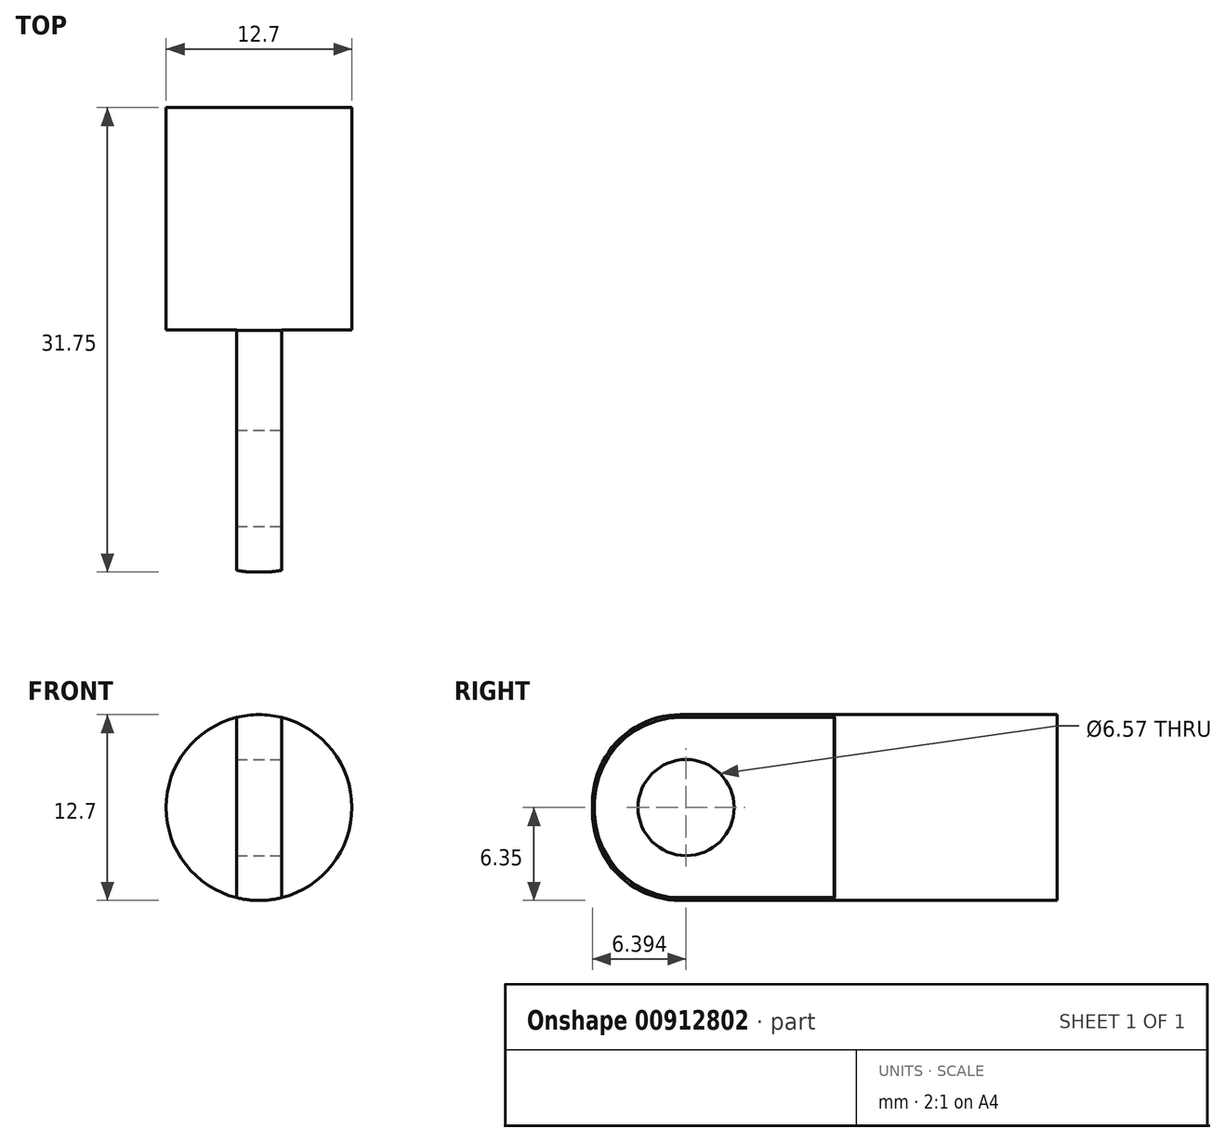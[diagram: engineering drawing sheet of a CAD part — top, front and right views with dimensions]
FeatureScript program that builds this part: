
annotation { "Feature Type Name" : "Feature", "Feature Type Description" : "" }
export const myFeature = defineFeature(function(context is Context, id is Id, definition is map)
    precondition{}
    {
        {
            var Q0;
            Q0=qCreatedBy(makeId("Front.planeOp"),FACE);
            var sketch = newSketch(context, id + "F0", { "sketchPlane" : qUnion([Q0])});
            skCircle(sketch, "E0", {"center": v(0, 0) * mm, "radius": 6.35 * mm});
            skSolve(sketch);
        }
        {
            var Q0;
            Q0 = qSketchRegion(id + "F0", true);
            extrude(context, id + "F1", {"entities" : qUnion([Q0]), "depth" : 31.75 * mm, "offsetDistance" : 25.4 * mm});
        }
        {
            var Q0;
            Q0=makeQuery(id+"F1.opExtrude","CAP_EDGE",EDGE,{"disambiguationData":[OSD([sQuery(id+"F0.wireOp",EDGE,"E0")])],"isStart":false});
            fillet(context, id + "F2", {"entities" : qUnion([Q0]), "radius" : 6.25 * mm, "tangentPropagation" : true, "allowEdgeOverflow" : false});
        }
        {
            var Q0;
            Q0=qCreatedBy(makeId("Top.planeOp"),FACE);
            var sketch = newSketch(context, id + "F3", { "sketchPlane" : qUnion([Q0])});
            skLineSegment(sketch, "E1.bottom", {"start": v(0, -35.56) * mm, "end": v(-1.54, -35.56) * mm});
            skLineSegment(sketch, "E1.top", {"start": v(0, -25.4) * mm, "end": v(-1.54, -25.4) * mm});
            skLineSegment(sketch, "E1.left", {"start": v(0, -35.56) * mm, "end": v(0, -25.4) * mm});
            skLineSegment(sketch, "E1.right", {"start": v(-1.54, -35.56) * mm, "end": v(-1.54, -25.4) * mm});
            skLineSegment(sketch, "E2.MirrorCS", {"start": v(0, -35.56) * mm, "end": v(1.54, -35.56) * mm});
            skLineSegment(sketch, "E3.MirrorCS", {"start": v(1.54, -35.56) * mm, "end": v(1.54, -25.4) * mm});
            skLineSegment(sketch, "E4.MirrorCS", {"start": v(0, -25.4) * mm, "end": v(1.54, -25.4) * mm});
            skLineSegment(sketch, "E5.MirrorCS", {"start": v(0, -15.24) * mm, "end": v(-1.54, -15.24) * mm});
            skLineSegment(sketch, "E6.MirrorCS", {"start": v(0, -15.24) * mm, "end": v(0, -25.4) * mm});
            skLineSegment(sketch, "E7.MirrorCS", {"start": v(-1.54, -15.24) * mm, "end": v(-1.54, -25.4) * mm});
            skLineSegment(sketch, "E8.MirrorCS", {"start": v(1.54, -15.24) * mm, "end": v(1.54, -25.4) * mm});
            skLineSegment(sketch, "E9.MirrorCS", {"start": v(0, -15.24) * mm, "end": v(1.54, -15.24) * mm});
            skSolve(sketch);
        }
        {
            var Q0;
            Q0 = qSketchRegion(id + "F3", true);
            var Q1;
            Q1 = qSketchRegion(id + "F5", true);
            extrude(context, id + "F4", {"entities" : qUnion([Q0, Q1]), "operationType" : NewBodyOperationType.REMOVE, "endBound" : BoundingType.SYMMETRIC, "oppositeDirection" : true, "depth" : 46.28 * mm, "offsetDistance" : 25.4 * mm});
        }
        {
            var Q0;
            Q0=qCreatedBy(makeId("Right.planeOp"),FACE);
            var sketch = newSketch(context, id + "F5", { "sketchPlane" : qUnion([Q0])});
            skCircle(sketch, "E10", {"center": v(-25.5, 0) * mm, "radius": 2.23 * mm});
            skCircle(sketch, "E11", {"center": v(-25.5, 0) * mm, "radius": 2.58 * mm});
            skSolve(sketch);
        }
        {
            var Q0;
            Q0=makeQuery(id+"F5.imprint","IMPRINT",FACE,{"disambiguationData":[TD([[makeQuery(id+"F5.imprint","IMPRINT",EDGE,{"derivedFrom":sQuery(id+"F5.wireOp",EDGE,"E10")}),1.0]])]});
            extrude(context, id + "F6", {"entities" : qUnion([Q0]), "operationType" : NewBodyOperationType.ADD, "endBound" : BoundingType.SYMMETRIC, "depth" : 5.03 * mm, "offsetDistance" : 25.4 * mm});
        }
        {
            var Q0;
            Q0=qCreatedBy(makeId("Top.planeOp"),FACE);
            var sketch = newSketch(context, id + "F7", { "sketchPlane" : qUnion([Q0])});
            skLineSegment(sketch, "E12.bottom", {"start": v(-1.54, -15.2) * mm, "end": v(-9.34, -15.2) * mm});
            skLineSegment(sketch, "E12.top", {"start": v(-1.54, -35.55) * mm, "end": v(-9.34, -35.55) * mm});
            skLineSegment(sketch, "E12.left", {"start": v(-1.54, -15.2) * mm, "end": v(-1.54, -35.55) * mm});
            skLineSegment(sketch, "E12.right", {"start": v(-9.34, -15.2) * mm, "end": v(-9.34, -35.55) * mm});
            skLineSegment(sketch, "E13.MirrorCS", {"start": v(1.54, -15.2) * mm, "end": v(1.54, -35.55) * mm});
            skLineSegment(sketch, "E14.MirrorCS", {"start": v(1.54, -35.55) * mm, "end": v(9.34, -35.55) * mm});
            skLineSegment(sketch, "E15.MirrorCS", {"start": v(1.54, -15.2) * mm, "end": v(9.34, -15.2) * mm});
            skLineSegment(sketch, "E16.MirrorCS", {"start": v(9.34, -15.2) * mm, "end": v(9.34, -35.55) * mm});
            skSolve(sketch);
        }
        {
            var Q0;
            Q0 = qSketchRegion(id + "F0", true);
            extrude(context, id + "F8", {"entities" : qUnion([Q0]), "depth" : 31.75 * mm, "offsetDistance" : 25.4 * mm});
        }
        {
            var Q0;
            Q0=makeQuery(id+"F8.opExtrude","CAP_EDGE",EDGE,{"disambiguationData":[OSD([sQuery(id+"F0.wireOp",EDGE,"E0")])],"isStart":false});
            fillet(context, id + "F9", {"entities" : qUnion([Q0]), "radius" : 6 * mm, "tangentPropagation" : true, "allowEdgeOverflow" : false});
        }
        {
            var Q0;
            Q0 = qSketchRegion(id + "F7", true);
            extrude(context, id + "F10", {"entities" : qUnion([Q0]), "operationType" : NewBodyOperationType.REMOVE, "endBound" : BoundingType.SYMMETRIC, "oppositeDirection" : true, "depth" : 25.4 * mm, "offsetDistance" : 25.4 * mm});
        }
        {
            var Q0;
            Q0=qCreatedBy(makeId("Right.planeOp"),FACE);
            var sketch = newSketch(context, id + "F11", { "sketchPlane" : qUnion([Q0])});
            skCircle(sketch, "E17", {"center": v(-25.36, 0) * mm, "radius": 3.29 * mm});
            skSolve(sketch);
        }
        {
            var Q0;
            Q0 = qSketchRegion(id + "F11", true);
            extrude(context, id + "F12", {"entities" : qUnion([Q0]), "operationType" : NewBodyOperationType.REMOVE, "endBound" : BoundingType.SYMMETRIC, "oppositeDirection" : true, "depth" : 38.46 * mm, "offsetDistance" : 25.4 * mm});
        }
    });
